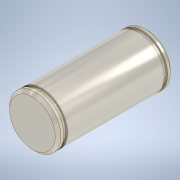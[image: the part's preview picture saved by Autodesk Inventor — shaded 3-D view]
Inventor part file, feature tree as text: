
AUTODESK INVENTOR PART (.ipt)
format: ipt  version: 2022 (Build 260153000, 153)  size: 139,776 bytes
history: native  units: mm
features: revolve x1, sketch x1
ambient origin geometry x8: Origin, YZ Plane, XZ Plane, XY Plane, X Axis, Y Axis, Z Axis, Center Point
bodies: Solid1 (feature_tree)
feature tree (2):
  revolve  "Revolution1"  [1 undecoded]
  sketch  "Sketch1"  dims[d0=2.0mm d2=1.2mm d3=1.0mm d4=135.0deg d5=9.0mm d7=17.0mm d8=90.0deg d11=0.5mm]
note: 1 required parameter value undecoded (feature->parameter linkage not recoverable at this tier; creation-order binding heuristic only, values carry confidence <= 0.55)
